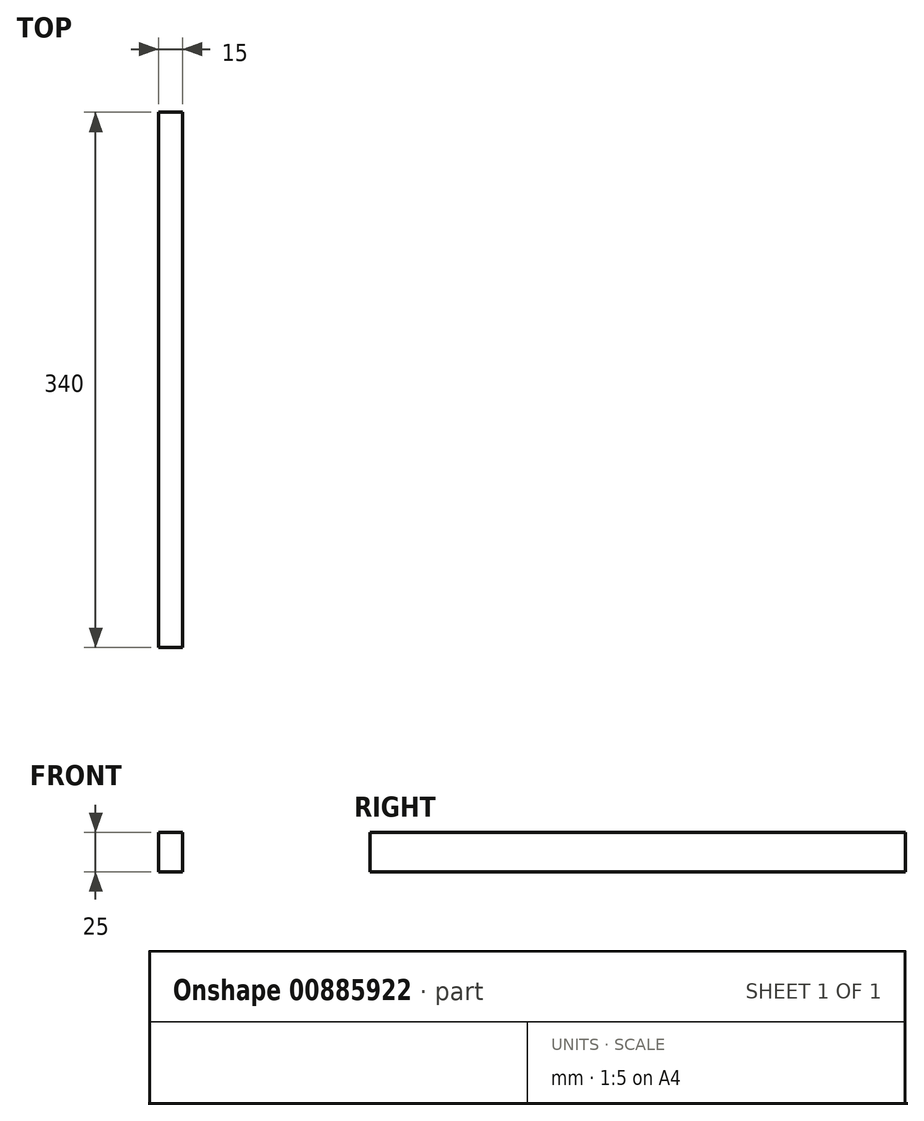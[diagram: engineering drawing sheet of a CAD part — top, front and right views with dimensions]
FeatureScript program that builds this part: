
annotation { "Feature Type Name" : "Feature", "Feature Type Description" : "" }
export const myFeature = defineFeature(function(context is Context, id is Id, definition is map)
    precondition{}
    {
        {
            var Q0;
            Q0=qCreatedBy(makeId("Front.planeOp"),FACE);
            var sketch = newSketch(context, id + "F0", { "sketchPlane" : qUnion([Q0])});
            skLineSegment(sketch, "E0.bottom", {"start": v(7.5, 12.5) * mm, "end": v(-7.5, 12.5) * mm});
            skLineSegment(sketch, "E0.top", {"start": v(7.5, -12.5) * mm, "end": v(-7.5, -12.5) * mm});
            skLineSegment(sketch, "E0.left", {"start": v(7.5, 12.5) * mm, "end": v(7.5, -12.5) * mm});
            skLineSegment(sketch, "E0.right", {"start": v(-7.5, 12.5) * mm, "end": v(-7.5, -12.5) * mm});
            skPoint(sketch, "E0.middle", {"position": v(0, 0) * mm});
            skSolve(sketch);
        }
        {
            var Q0;
            Q0 = qSketchRegion(id + "F0", true);
            extrude(context, id + "F1", {"entities" : qUnion([Q0]), "oppositeDirection" : true, "depth" : 340 * mm, "offsetDistance" : 25 * mm});
        }
    });
